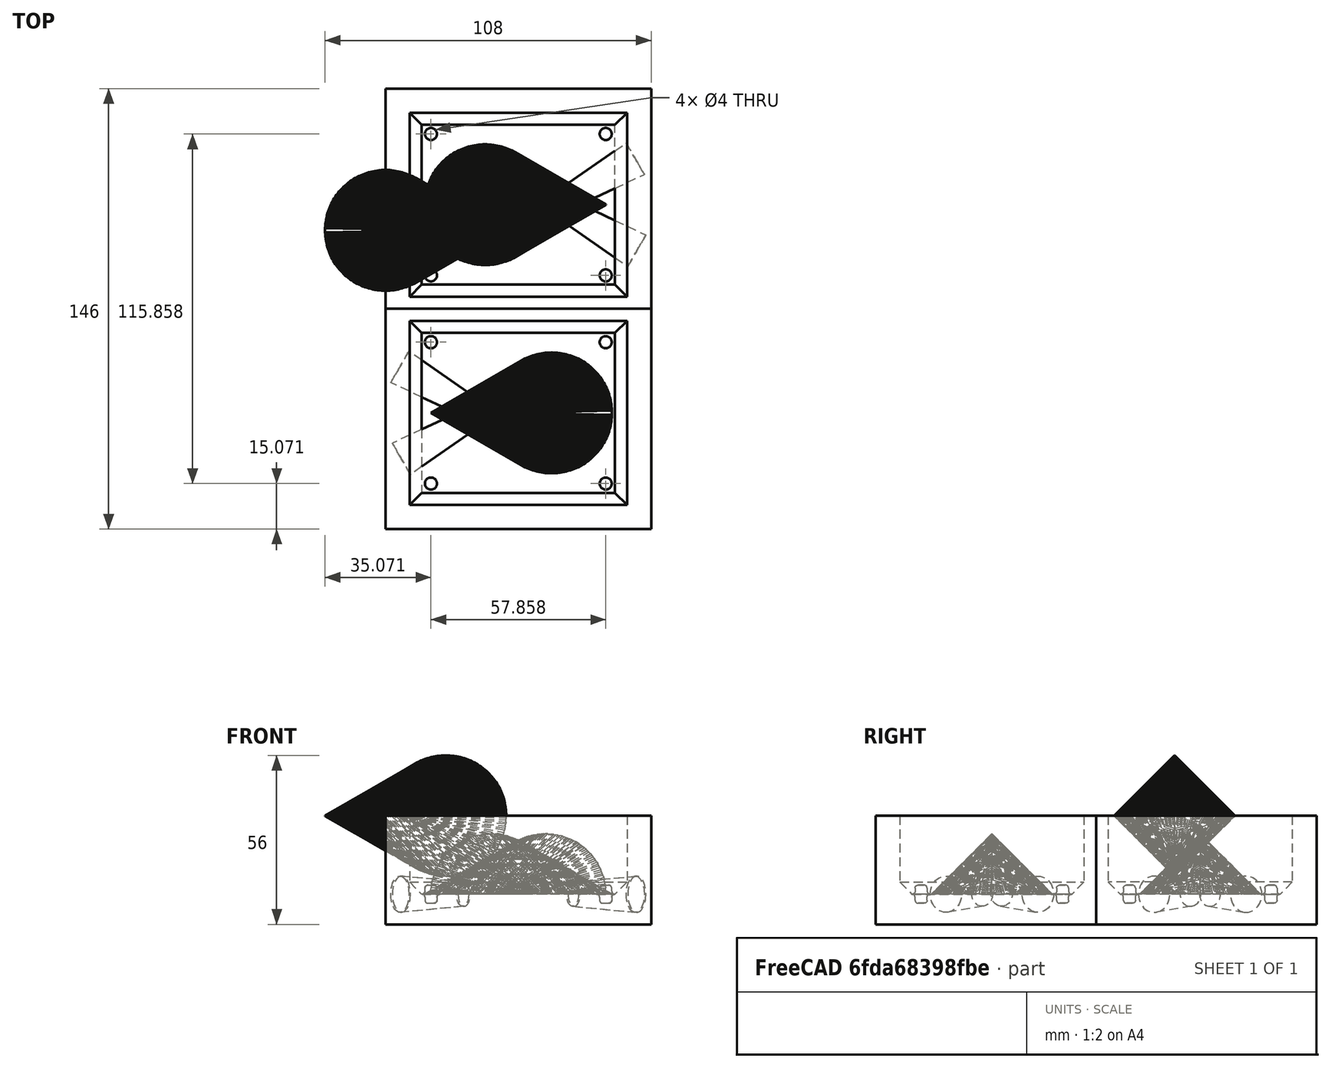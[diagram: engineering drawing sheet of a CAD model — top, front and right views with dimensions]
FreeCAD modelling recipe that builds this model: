
FCSTD DOCUMENT  (FreeCAD 0.19R22474 (Git))
Label: oloid-model-2
License: All rights reserved
LicenseURL: http://en.wikipedia.org/wiki/All_rights_reserved
objects: Sketcher::SketchObject×7, Part::Feature×3, Part::Compound×3, Mesh::Feature×2, Part::Extrusion×2, Part::Cut×2, PartDesign::Pad×2, PartDesign::Pocket×2, Part::Cone×2, PartDesign::Body×2, Spreadsheet::Sheet×1, Part::Refine×1, PartDesign::Chamfer×1, PartDesign::Fillet×1, PartDesign::FeatureBase×1
note: 35 computed .brp shape members not serialized (recipe doc carries the construction recipe); baked Part::Feature solids carry a one-line shape summary decoded from their .brp

FEATURE [Mesh::Feature] oloid
  Placement = pos=(-44,26,0) rot=(0,0,1;0rad)
FEATURE [Spreadsheet::Sheet] Spreadsheet
  cells = A1=wax_height; B1(wax_height)==36mm; A2=wax_width; B2(wax_width)==88mm; A3=wax_length; B3(wax_length)==146mm; A4=wax_margin; B4(wax_margin)==8mm; A5=wax_mark_dia; B5(wax_mark_dia)==4mm; A6=wax_mark_filet; B6(wax_mark_filet)==1mm; A7=wax_mark_margin; B7(wax_mark_margin)==10mm; A8=wax_mark_height; B8(wax_mark_height)==3mm; A9=wax_chamfer; B9(wax_chamfer)==4mm
FEATURE [Part::Feature] oloid001001
  shape: bbox 60 x 40 x 40 mm, 964 faces, 0 solids (baked)
FEATURE [Mesh::Feature] oloid001  label="oloid-top"
  Placement = pos=(-44,26,0) rot=(0,0,1;0rad)
FEATURE [Part::Refine] oloid001001001
  Source = -> oloid001001
FEATURE [Sketcher::SketchObject] Sketch001
  MapMode = 7
  Placement = pos=(-40.527,45.6962,0.05) rot=(-0.503589,0.6109,0.6109;4.07462rad)
  Support = -> [oloid001001001]
  sketch-geometry (4):
    g0: LineSegment StartX=-18.1967 StartY=0 StartZ=0 EndX=49.034 EndY=0 EndZ=0
    g1: LineSegment StartX=49.034 StartY=0 StartZ=0 EndX=49.034 EndY=-26.9691 EndZ=0
    g2: LineSegment StartX=49.034 StartY=-26.9691 StartZ=0 EndX=-18.1967 EndY=-26.9691 EndZ=0
    g3: LineSegment StartX=-18.1967 StartY=-26.9691 StartZ=0 EndX=-18.1967 EndY=0 EndZ=0
  constraints (9):
    c: Coincident(g0,g1)
    c: Coincident(g1,g2)
    c: Coincident(g2,g3)
    c: Coincident(g3,g0)
    c: Horizontal(g0)
    c: Horizontal(g2)
    c: Vertical(g1)
    c: Vertical(g3)
    c: PointOnObject(g0,g-1)
FEATURE [Part::Extrusion] Extrude
  Base = -> Sketch001
  Dir = (-0.981628,0.190804,1e-16)
  DirMode = 2
  FaceMakerClass = Part::FaceMakerBullseye
  LengthFwd = 100
  LengthRev = 100
  Solid = true
  Symmetric = false
FEATURE [Part::Feature] oloid001001001_solid  label="oloid001001001 (Solid)"
  shape: bbox 60 x 40 x 40 mm, 724 faces (baked)
FEATURE [Part::Feature] oloid001001001_solid001  label="oloid001001001 (Solid)001"
  shape: bbox 60 x 40 x 40 mm, 724 faces (baked)
FEATURE [Part::Cut] Cut  label="o-top"
  Base = -> oloid001001001_solid001
  Placement = pos=(33,8.5,-26) rot=(0,0,1;0rad)
  Tool = -> Extrude
FEATURE [Sketcher::SketchObject] Sketch003
  MapMode = 5
  Support = -> [XY_Plane002]
  expr: Constraints[6] = Spreadsheet.wax_width
  expr: Constraints[7] = Spreadsheet.wax_length
  sketch-geometry (4):
    g0: LineSegment StartX=-44 StartY=73 StartZ=0 EndX=44 EndY=73 EndZ=0
    g1: LineSegment StartX=44 StartY=73 StartZ=0 EndX=44 EndY=-73 EndZ=0
    g2: LineSegment StartX=44 StartY=-73 StartZ=0 EndX=-44 EndY=-73 EndZ=0
    g3: LineSegment StartX=-44 StartY=-73 StartZ=0 EndX=-44 EndY=73 EndZ=0
  constraints (10):
    c: Coincident(g0,g1)
    c: Coincident(g1,g2)
    c: Coincident(g2,g3)
    c: Coincident(g3,g0)
    c: Horizontal(g2)
    c: Vertical(g3)
    c: DistanceX(g2,g2) = 88
    c: DistanceY(g3,g3) = 146
    c: Symmetric(g0,g0,g-2)
    c: Symmetric(g0,g1,g-1)
FEATURE [PartDesign::Pad] Pad001
  Direction = (1,1,1)
  Length = 36
  Length2 = 100
  Profile = -> Sketch003
  Reversed = true
  Type = 0
  expr: Length = Spreadsheet.wax_height
FEATURE [Sketcher::SketchObject] Sketch004
  ExternalGeometry = -> [Pad001]
  MapMode = 5
  Support = -> [Pad001]
  expr: Constraints[34] = Spreadsheet.wax_margin
  sketch-geometry (15):
    g0: LineSegment StartX=-36 StartY=-65 StartZ=0 EndX=36 EndY=-65 EndZ=0
    g1: LineSegment StartX=36 StartY=-65 StartZ=0 EndX=36 EndY=-4 EndZ=0
    g2: LineSegment StartX=36 StartY=-4 StartZ=0 EndX=-36 EndY=-4 EndZ=0
    g3: LineSegment StartX=-36 StartY=-4 StartZ=0 EndX=-36 EndY=-65 EndZ=0
    g4: LineSegment StartX=-36 StartY=4 StartZ=0 EndX=36 EndY=4 EndZ=0
    g5: LineSegment StartX=36 StartY=4 StartZ=0 EndX=36 EndY=65 EndZ=0
    g6: LineSegment StartX=36 StartY=65 StartZ=0 EndX=-36 EndY=65 EndZ=0
    g7: LineSegment StartX=-36 StartY=65 StartZ=0 EndX=-36 EndY=4 EndZ=0
    g8: LineSegment [constr] StartX=-11.1504 StartY=65 StartZ=0 EndX=-11.1504 EndY=73 EndZ=0
    g9: LineSegment [constr] StartX=36 StartY=44.7237 StartZ=0 EndX=44 EndY=44.7237 EndZ=0
    g10: LineSegment [constr] StartX=-36 StartY=42.4369 StartZ=0 EndX=-44 EndY=42.4369 EndZ=0
    g11: LineSegment [constr] StartX=-36 StartY=-28.7388 StartZ=0 EndX=-44 EndY=-28.7388 EndZ=0
    g12: LineSegment [constr] StartX=-12.0079 StartY=-65 StartZ=0 EndX=-12.0079 EndY=-73 EndZ=0
    g13: LineSegment [constr] StartX=36 StartY=-43.4599 StartZ=0 EndX=44 EndY=-43.4599 EndZ=0
    g14: LineSegment [constr] StartX=-16.4572 StartY=4 StartZ=0 EndX=-16.4572 EndY=-4 EndZ=0
  constraints (45):
    c: Coincident(g0,g1)
    c: Coincident(g1,g2)
    c: Coincident(g2,g3)
    c: Coincident(g3,g0)
    c: Horizontal(g0)
    c: Horizontal(g2)
    c: Vertical(g1)
    c: Vertical(g3)
    c: Coincident(g4,g5)
    c: Coincident(g5,g6)
    c: Coincident(g6,g7)
    c: Coincident(g7,g4)
    c: Horizontal(g4)
    c: Horizontal(g6)
    c: Vertical(g5)
    c: Vertical(g7)
    c: PointOnObject(g8,g6)
    c: PointOnObject(g8,g-3)
    c: Vertical(g8)
    c: PointOnObject(g9,g5)
    c: PointOnObject(g9,g-4)
    c: Horizontal(g9)
    c: PointOnObject(g10,g7)
    c: PointOnObject(g10,g-6)
    c: Horizontal(g10)
    c: PointOnObject(g11,g3)
    c: PointOnObject(g11,g-6)
    c: Horizontal(g11)
    c: PointOnObject(g12,g0)
    c: PointOnObject(g12,g-5)
    c: Vertical(g12)
    c: PointOnObject(g13,g1)
    c: PointOnObject(g13,g-4)
    c: Horizontal(g13)
    c: DistanceY(g8,g8) = 8
    c: Equal(g8,g10)
    c: Equal(g11,g12)
    c: Equal(g12,g13)
    c: Equal(g13,g8)
    c: PointOnObject(g14,g4)
    c: PointOnObject(g14,g2)
    c: Equal(g14,g10)
    c: Symmetric(g14,g14,g-1)
    c: Equal(g9,g8)
    c: Equal(g14,g8)
FEATURE [PartDesign::Pocket] Pocket001
  BaseFeature = -> Pad001
  Length = 26
  Length2 = 100
  Profile = -> Sketch004
  Type = 0
FEATURE [Part::Cone] Cone
  Angle = 360
  AttacherType = Attacher::AttachEngine3D
  Height = 24
  Placement = pos=(17.9522,37.7194,-26) rot=(0.694747,0.186157,0.694747;3.50969rad)
  Radius1 = 4
  Radius2 = 6
FEATURE [Sketcher::SketchObject] Sketch  label="oloid-frame"
  MapMode = 5
  Placement = pos=(0,0,-26) rot=(0,0,1;0rad)
  Support = -> [Pocket001]
  sketch-geometry (4):
    g0: LineSegment StartX=-31.0026 StartY=54.4987 StartZ=0 EndX=29 EndY=54.4987 EndZ=0
    g1: LineSegment StartX=29 StartY=54.4987 StartZ=0 EndX=29 EndY=14.4898 EndZ=0
    g2: LineSegment StartX=29 StartY=14.4898 StartZ=0 EndX=-31.0026 EndY=14.4898 EndZ=0
    g3: LineSegment StartX=-31.0026 StartY=14.4898 StartZ=0 EndX=-31.0026 EndY=54.4987 EndZ=0
  constraints (8):
    c: Coincident(g0,g1)
    c: Coincident(g1,g2)
    c: Coincident(g2,g3)
    c: Coincident(g3,g0)
    c: Horizontal(g0)
    c: Horizontal(g2)
    c: Vertical(g1)
    c: Vertical(g3)
FEATURE [Sketcher::SketchObject] Sketch005
  ExternalGeometry = -> [Pocket001]
  MapMode = 5
  Placement = pos=(0,0,-26) rot=(0,0,1;0rad)
  Support = -> [Pocket001]
  expr: Constraints[4] = Spreadsheet.wax_mark_margin
  expr: Constraints[0] = Spreadsheet.wax_mark_dia
  sketch-geometry (4):
    g0: Circle CenterX=-28.9289 CenterY=57.9289 CenterZ=0 NormalX=0 NormalY=0 NormalZ=1 AngleXU=0 Radius=2
    g1: Circle CenterX=28.9289 CenterY=11.0711 CenterZ=0 NormalX=0 NormalY=0 NormalZ=1 AngleXU=0 Radius=2
    g2: LineSegment [constr] StartX=-28.9289 StartY=57.9289 StartZ=0 EndX=-36 EndY=65 EndZ=0
    g3: LineSegment [constr] StartX=28.9289 StartY=11.0711 StartZ=0 EndX=36 EndY=4 EndZ=0
  constraints (10):
    c: Diameter(g0) = 4
    c: Coincident(g2,g0)
    c: Coincident(g2,g-4)
    c: Angle(g2,g-4) = 0.785398
    c: Distance(g2) = 10
    c: Coincident(g3,g1)
    c: Coincident(g3,g-6)
    c: Angle(g-5,g3) = 0.785398
    c: Equal(g3,g2)
    c: Equal(g1,g0)
FEATURE [PartDesign::Pocket] Pocket
  BaseFeature = -> Pocket001
  Length = 3
  Length2 = 100
  Profile = -> Sketch005
  Type = 0
  expr: Length = Spreadsheet.wax_mark_height
FEATURE [Sketcher::SketchObject] Sketch006
  ExternalGeometry = -> [Pocket]
  MapMode = 5
  Placement = pos=(0,0,-26) rot=(0,0,1;0rad)
  Support = -> [Pocket]
  expr: Constraints[0] = Spreadsheet.wax_mark_dia
  expr: Constraints[9] = Spreadsheet.wax_mark_margin
  sketch-geometry (4):
    g0: Circle CenterX=28.9289 CenterY=57.9289 CenterZ=0 NormalX=0 NormalY=0 NormalZ=1 AngleXU=0 Radius=2
    g1: Circle CenterX=-28.9289 CenterY=11.0711 CenterZ=0 NormalX=0 NormalY=0 NormalZ=1 AngleXU=0 Radius=2
    g2: LineSegment [constr] StartX=28.9289 StartY=57.9289 StartZ=0 EndX=36 EndY=65 EndZ=0
    g3: LineSegment [constr] StartX=-28.9289 StartY=11.0711 StartZ=0 EndX=-36 EndY=4 EndZ=0
  constraints (11):
    c: Diameter(g1) = 4
    c: Equal(g0,g1)
    c: Coincident(g2,g0)
    c: Coincident(g2,g-4)
    c: Angle(g-3,g2) = 0.785398
    c: Coincident(g3,g1)
    c: Coincident(g3,g-6)
    c: Equal(g3,g2)
    c: Angle(g3,g-5) = 0.785398
    c: Distance(g3) = 10
    c: Equal(g2,g3)
FEATURE [PartDesign::Pad] Pad
  BaseFeature = -> Pocket
  Direction = (1,1,1)
  Length = 3
  Length2 = 100
  Profile = -> Sketch006
  Type = 0
  expr: Length = Spreadsheet.wax_mark_height
FEATURE [PartDesign::Chamfer] Chamfer
  Angle = 45
  Base = -> Pad [Edge31,Edge33,Edge35,Edge36]
  BaseFeature = -> Pad
  ChamferType = 0
  FlipDirection = false
  Size = 4
  Size2 = 1
  SupportTransform = false
  expr: Size = Spreadsheet.wax_chamfer
FEATURE [PartDesign::Fillet] Fillet
  Base = -> Chamfer [Edge50,Edge28,Edge30,Edge54,Edge56,Edge31,Edge29,Edge52]
  BaseFeature = -> Chamfer
  Radius = 1
  SupportTransform = false
FEATURE [PartDesign::Body] Body002  label="wax001"
  Group = -> [Sketch003,Pad001,Sketch004,Pocket001,Sketch005,Pocket,Sketch006,Pad,Chamfer,Fillet]
  Origin = -> Origin002
  Tip = -> Fillet
FEATURE [Sketcher::SketchObject] Sketch007
  MapMode = 5
  Placement = pos=(0,0,-36) rot=(1,0,0;3.14159rad)
  Support = -> [Fillet]
  sketch-geometry (4):
    g0: LineSegment StartX=-55.8899 StartY=0 StartZ=0 EndX=59.1736 EndY=0 EndZ=0
    g1: LineSegment StartX=59.1736 StartY=0 StartZ=0 EndX=59.1736 EndY=79.4388 EndZ=0
    g2: LineSegment StartX=59.1736 StartY=79.4388 StartZ=0 EndX=-55.8899 EndY=79.4388 EndZ=0
    g3: LineSegment StartX=-55.8899 StartY=79.4388 StartZ=0 EndX=-55.8899 EndY=0 EndZ=0
  constraints (9):
    c: Coincident(g0,g1)
    c: Coincident(g1,g2)
    c: Coincident(g2,g3)
    c: Coincident(g3,g0)
    c: Horizontal(g0)
    c: Horizontal(g2)
    c: Vertical(g1)
    c: Vertical(g3)
    c: PointOnObject(g0,g-1)
FEATURE [Part::Extrusion] Extrude001
  Base = -> Sketch007
  Dir = (0,0,-1)
  DirMode = 2
  FaceMakerClass = Part::FaceMakerBullseye
  LengthFwd = -50
  LengthRev = -50
  Solid = true
  Symmetric = false
FEATURE [Part::Cut] Cut001
  Base = -> Body002
  Tool = -> Extrude001
FEATURE [Part::Cone] Cone001
  Angle = 360
  AttacherType = Attacher::AttachEngine3D
  Height = 24
  Placement = pos=(18.4518,31.2484,-26) rot=(-0.250563,-0.935113,0.250563;4.64535rad)
  Radius1 = 4
  Radius2 = 6
FEATURE [Part::Compound] Compound
  Links = -> [Cut,Sketch,Cone,Cone001]
FEATURE [Part::Compound] Compound001  label="oloid-1"
  Links = -> [Cut001,Compound]
FEATURE [PartDesign::FeatureBase] Clone
  BaseFeature = -> Compound001
FEATURE [PartDesign::Body] Body  label="clone"
  BaseFeature = -> Compound001
  Group = -> [Clone]
  Origin = -> Origin
  Placement = pos=(9.3e-15,0,0) rot=(0,0,1;3.14159rad)
  Tip = -> Clone
FEATURE [Part::Compound] Compound002
  Links = -> [Body,Compound001]
